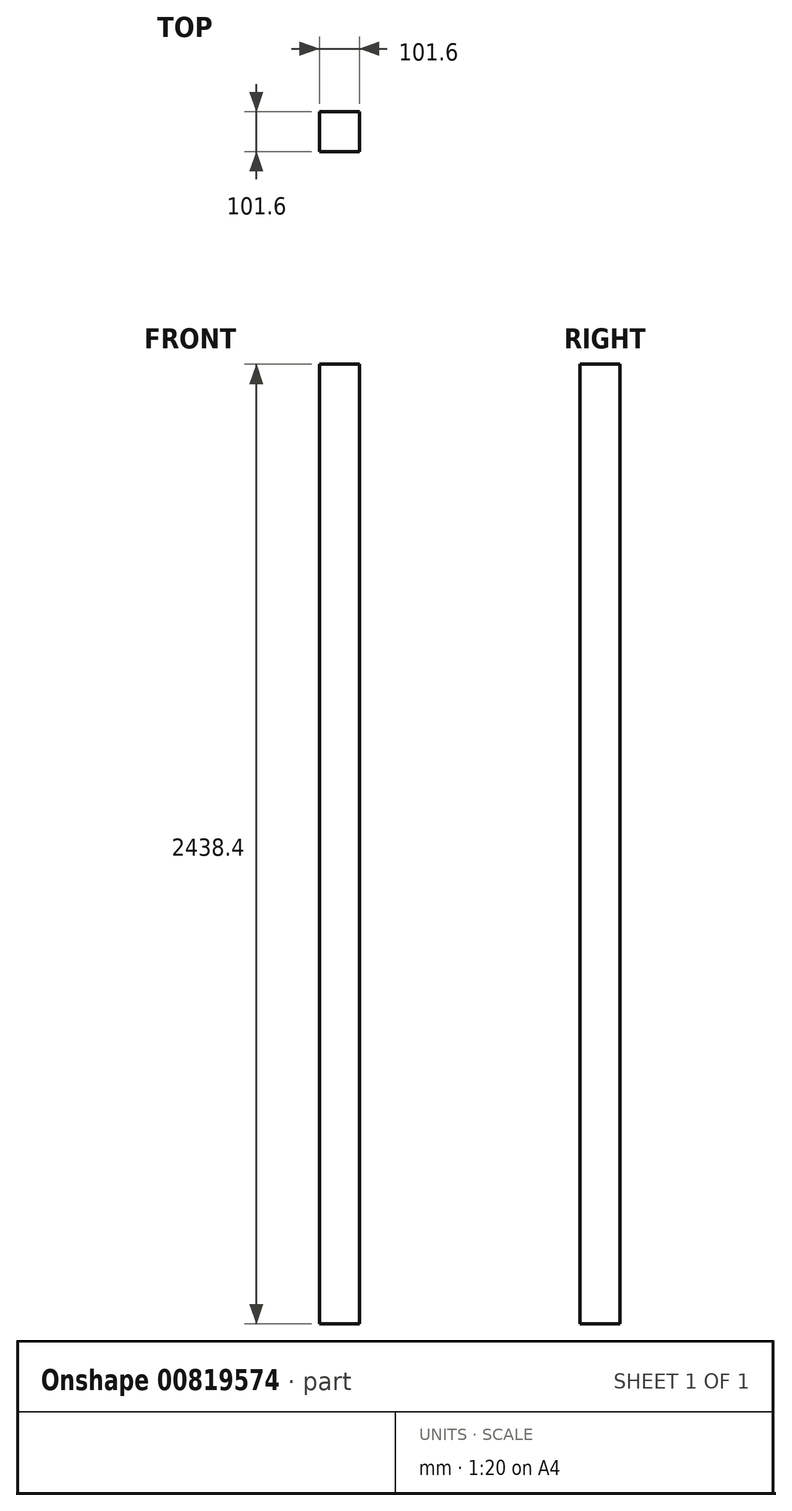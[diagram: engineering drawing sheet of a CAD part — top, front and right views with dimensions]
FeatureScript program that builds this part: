
annotation { "Feature Type Name" : "Feature", "Feature Type Description" : "" }
export const myFeature = defineFeature(function(context is Context, id is Id, definition is map)
    precondition{}
    {
        {
            var Q0;
            Q0=qCreatedBy(makeId("Top.planeOp"),FACE);
            var sketch = newSketch(context, id + "F0", { "sketchPlane" : qUnion([Q0])});
            skLineSegment(sketch, "E0.bottom", {"start": v(-50.8, 50.8) * mm, "end": v(50.8, 50.8) * mm});
            skLineSegment(sketch, "E0.top", {"start": v(-50.8, -50.8) * mm, "end": v(50.8, -50.8) * mm});
            skLineSegment(sketch, "E0.left", {"start": v(-50.8, 50.8) * mm, "end": v(-50.8, -50.8) * mm});
            skLineSegment(sketch, "E0.right", {"start": v(50.8, 50.8) * mm, "end": v(50.8, -50.8) * mm});
            skPoint(sketch, "E0.middle", {"position": v(0, 0) * mm});
            skSolve(sketch);
        }
        {
            var Q0;
            Q0 = qSketchRegion(id + "F0", true);
            extrude(context, id + "F1", {"entities" : qUnion([Q0]), "depth" : 2438.4 * mm, "offsetDistance" : 25.4 * mm});
        }
    });
